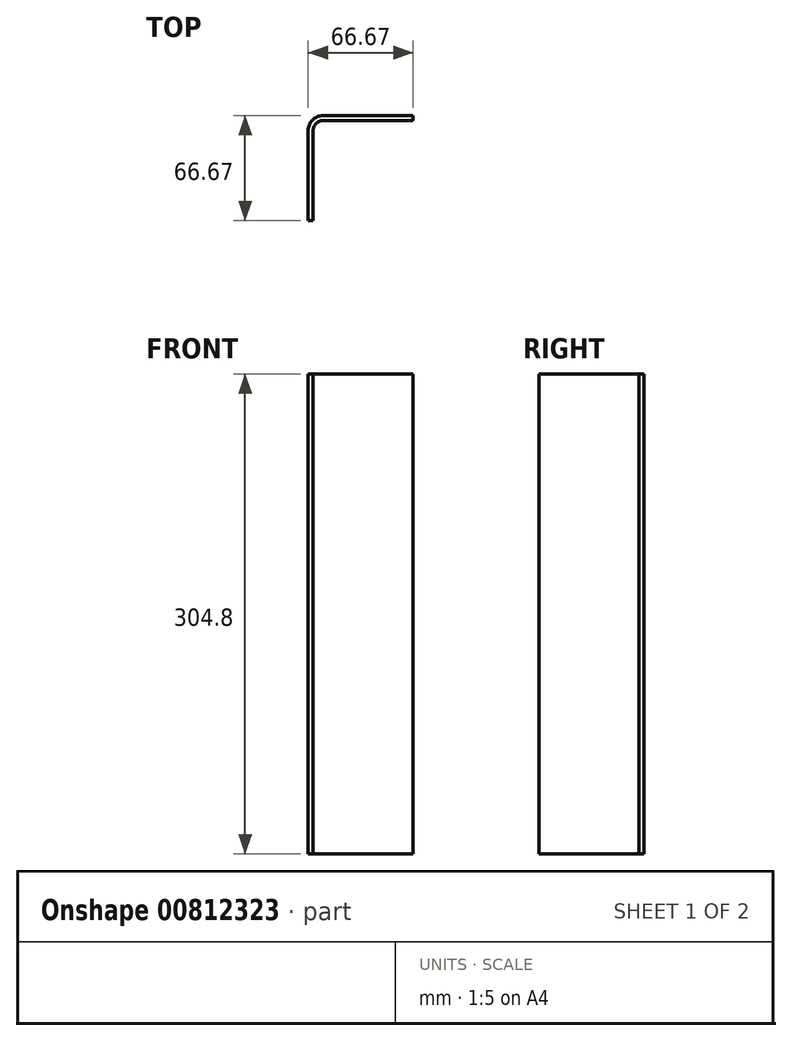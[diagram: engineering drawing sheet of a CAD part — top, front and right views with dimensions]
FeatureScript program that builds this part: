
annotation { "Feature Type Name" : "Feature", "Feature Type Description" : "" }
export const myFeature = defineFeature(function(context is Context, id is Id, definition is map)
    precondition{}
    {
        {
            var Q0;
            Q0=qCreatedBy(makeId("Top.planeOp"),FACE);
            var sketch = newSketch(context, id + "F0", { "sketchPlane" : qUnion([Q0])});
            skLineSegment(sketch, "E0.bottom", {"start": v(0, 0) * mm, "end": v(3.18, 0) * mm});
            skLineSegment(sketch, "E0.top", {"start": v(9.52, 66.67) * mm, "end": v(66.68, 66.67) * mm});
            skLineSegment(sketch, "E0.left", {"start": v(0, 0) * mm, "end": v(0, 57.15) * mm});
            skLineSegment(sketch, "E0.right", {"start": v(66.68, 63.5) * mm, "end": v(66.68, 66.67) * mm});
            skLineSegment(sketch, "E1.top", {"start": v(66.68, 63.5) * mm, "end": v(9.52, 63.5) * mm});
            skLineSegment(sketch, "E1.right", {"start": v(3.18, 0) * mm, "end": v(3.18, 57.15) * mm});
            skPoint(sketch, "E2.visualSharp", {"position": v(3.18, 63.5) * mm});
            skArc(sketch, "E2.filletArc", {"start": v(9.52, 63.5) * mm, "mid": v(5.03, 61.64) * mm, "end": v(3.17, 57.15) * mm});
            skPoint(sketch, "E3.visualSharp", {"position": v(0, 66.67) * mm});
            skArc(sketch, "E3.filletArc", {"start": v(9.52, 66.67) * mm, "mid": v(2.79, 63.89) * mm, "end": v(0, 57.15) * mm});
            skSolve(sketch);
        }
        {
            var Q0;
            Q0 = qSketchRegion(id + "F0", true);
            extrude(context, id + "F1", {"entities" : qUnion([Q0]), "depth" : 304.8 * mm, "offsetDistance" : 25.4 * mm});
        }
    });
